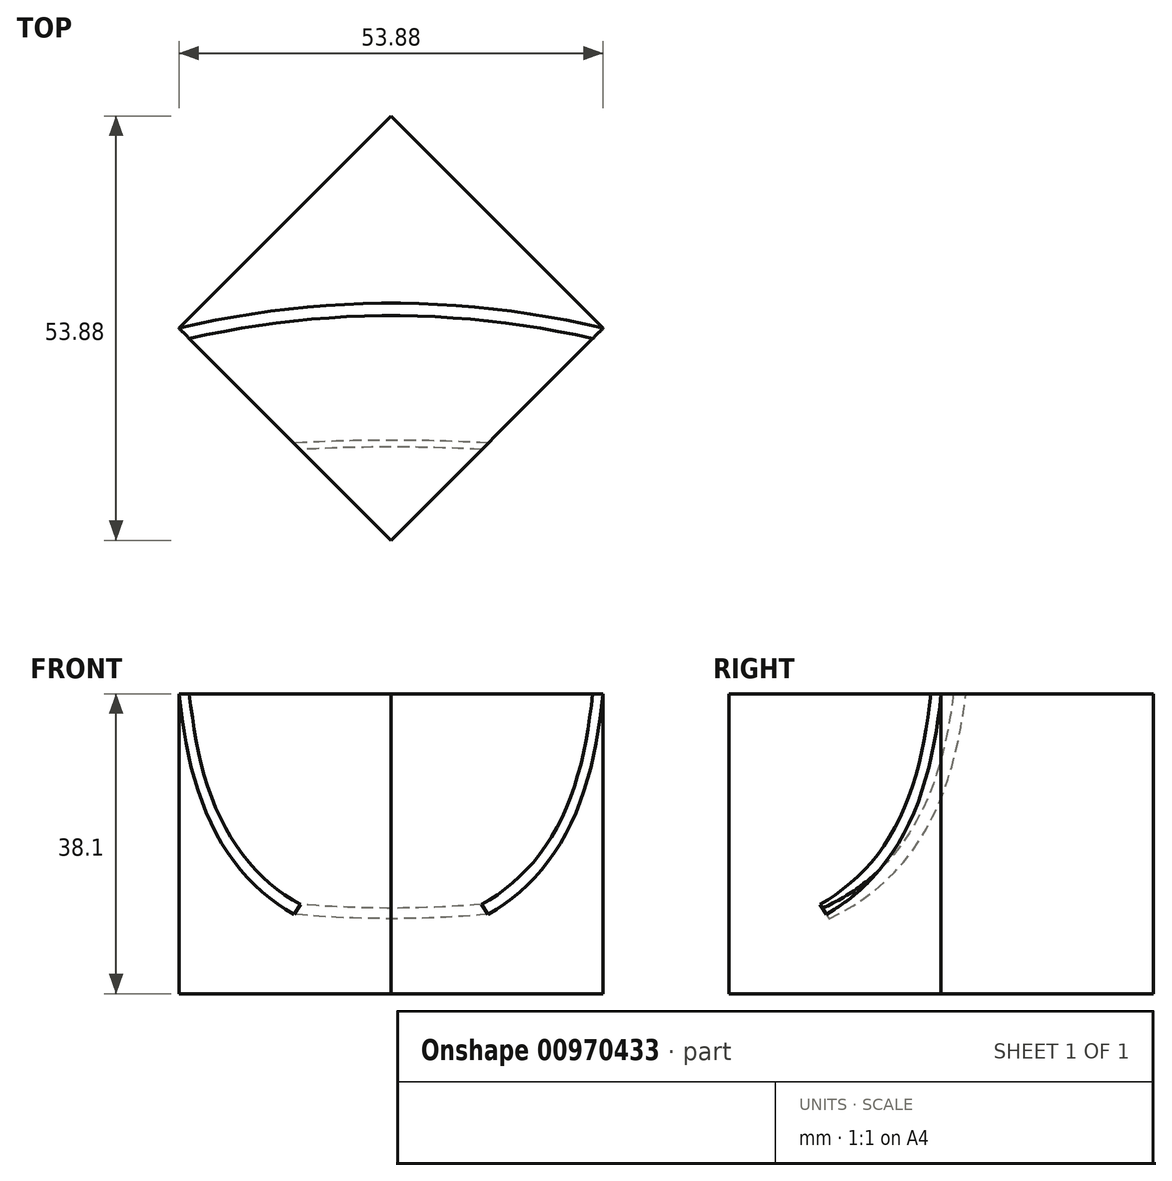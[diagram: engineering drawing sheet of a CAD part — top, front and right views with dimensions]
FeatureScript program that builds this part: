
annotation { "Feature Type Name" : "Feature", "Feature Type Description" : "" }
export const myFeature = defineFeature(function(context is Context, id is Id, definition is map)
    precondition{}
    {
        {
            var Q0;
            Q0=qCreatedBy(makeId("Top.planeOp"),FACE);
            var sketch = newSketch(context, id + "F0", { "sketchPlane" : qUnion([Q0])});
            skLineSegment(sketch, "E0.bottom", {"start": v(26.94, 0) * mm, "end": v(0, -26.94) * mm});
            skLineSegment(sketch, "E0.top", {"start": v(0, 26.94) * mm, "end": v(-26.94, 0) * mm});
            skLineSegment(sketch, "E0.left", {"start": v(26.94, 0) * mm, "end": v(0, 26.94) * mm});
            skLineSegment(sketch, "E0.right", {"start": v(0, -26.94) * mm, "end": v(-26.94, 0) * mm});
            skPoint(sketch, "E0.middle", {"position": v(0, 0) * mm});
            skSolve(sketch);
        }
        {
            var Q0;
            Q0=makeQuery(id+"F0.imprint","IMPRINT",FACE,{"disambiguationData":[TD([[makeQuery(id+"F0.imprint","IMPRINT",EDGE,{"derivedFrom":sQuery(id+"F0.wireOp",EDGE,"E0.bottom")}),-1.0]])]});
            extrude(context, id + "F1", {"entities" : qUnion([Q0]), "depth" : 38.1 * mm, "offsetDistance" : 25.4 * mm});
        }
        {
            var Q0;
            Q0=qCreatedBy(makeId("Right.planeOp"),FACE);
            var sketch = newSketch(context, id + "F2", { "sketchPlane" : qUnion([Q0])});
            skFitSpline(sketch, "E1", {"points": [v(-14.24, 9.53) * mm, v(3.5, 40.05) * mm], "startDerivative": vector(48.69, 22.28) * mm, "endDerivative": vector(3.08, 14.87) * mm});
            skSolve(sketch);
        }
        {
            var Q0;
            Q0=makeQuery(id+"F1.opExtrude","CAP_FACE",FACE,{"disambiguationData":[OSD([sQuery(id+"F0.wireOp",EDGE,"E0.bottom"),sQuery(id+"F0.wireOp",EDGE,"E0.top"),sQuery(id+"F0.wireOp",EDGE,"E0.left"),sQuery(id+"F0.wireOp",EDGE,"E0.right")])],"isStart":false});
            var sketch = newSketch(context, id + "F3", { "sketchPlane" : qUnion([Q0])});
            skArc(sketch, "E2", {"start": v(26.94, 0) * mm, "mid": v(0, 3.18) * mm, "end": v(-26.94, 0) * mm});
            skArc(sketch, "E3.0", {"start": v(25.62, -1.32) * mm, "mid": v(0, 1.59) * mm, "end": v(-25.62, -1.32) * mm});
            skLineSegment(sketch, "E4", {"start": v(25.62, -1.32) * mm, "end": v(26.94, 0) * mm});
            skLineSegment(sketch, "E5", {"start": v(-25.62, -1.32) * mm, "end": v(-26.94, 0) * mm});
            skSolve(sketch);
        }
        {
            var Q0;
            Q0=makeQuery(id+"F3.imprint","IMPRINT",FACE,{"disambiguationData":[TD([[makeQuery(id+"F3.imprint","IMPRINT",EDGE,{"derivedFrom":sQuery(id+"F3.wireOp",EDGE,"E2")}),1.0]])]});
            var Q1;
            Q1=sQuery(id+"F2.wireOp",EDGE,"E1");
            sweep(context, id + "F4", {"operationType" : NewBodyOperationType.REMOVE, "profiles" : qUnion([Q0]), "path" : qUnion([Q1])});
        }
    });
